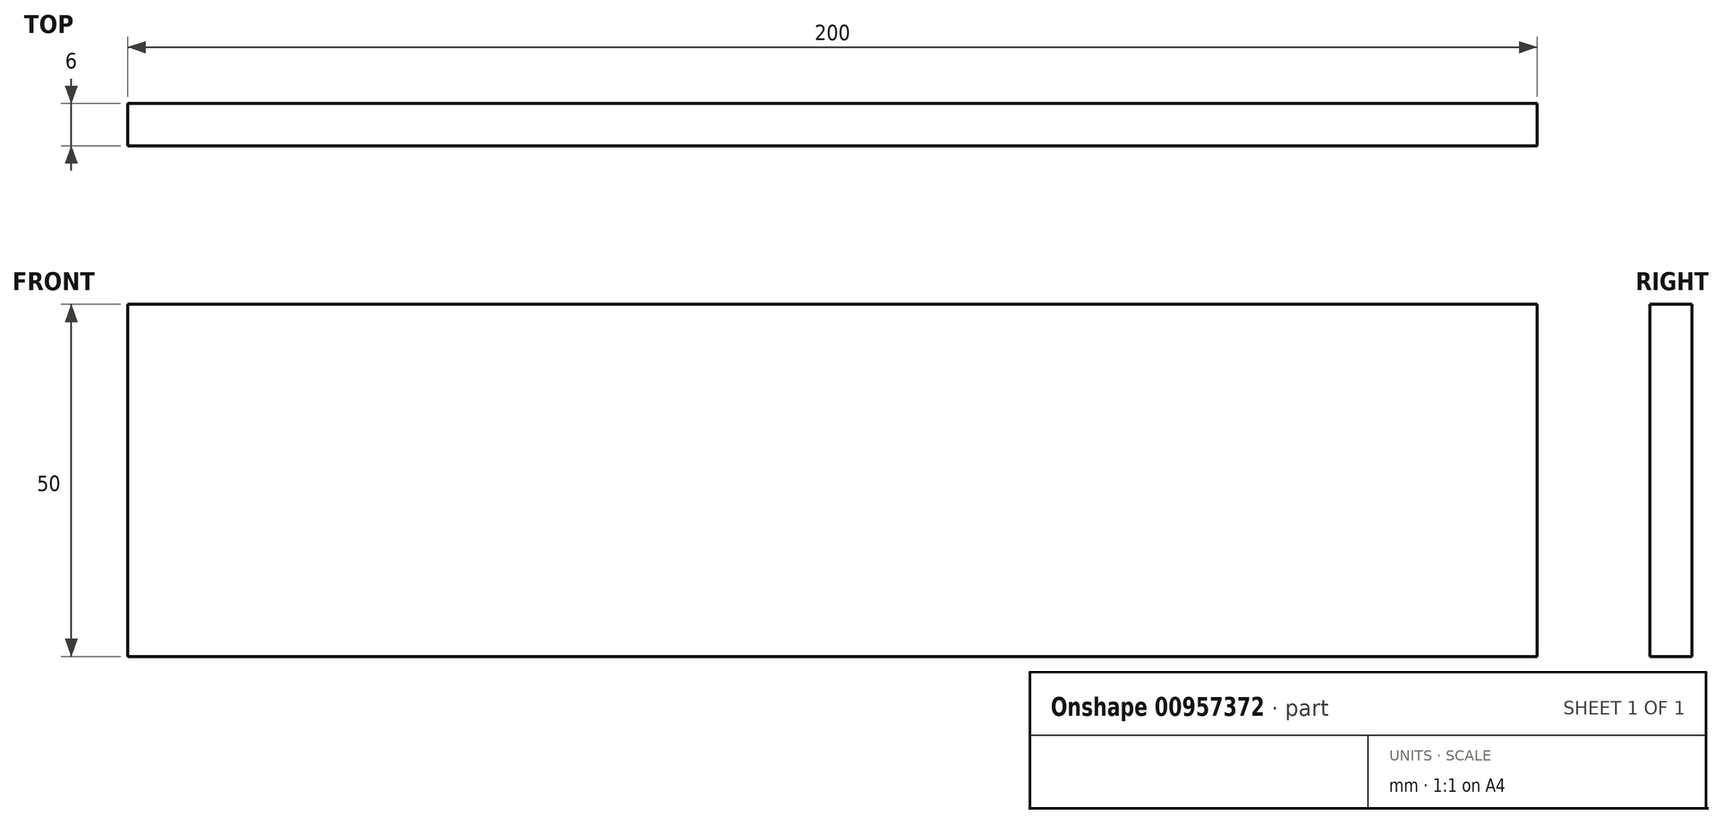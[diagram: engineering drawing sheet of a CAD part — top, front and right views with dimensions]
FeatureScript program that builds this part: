
annotation { "Feature Type Name" : "Feature", "Feature Type Description" : "" }
export const myFeature = defineFeature(function(context is Context, id is Id, definition is map)
    precondition{}
    {
        {
            var Q0;
            Q0=qCreatedBy(makeId("Front.planeOp"),FACE);
            var sketch = newSketch(context, id + "F0", { "sketchPlane" : qUnion([Q0])});
            skLineSegment(sketch, "E0.bottom", {"start": v(-68, 43.57) * mm, "end": v(132, 43.57) * mm});
            skLineSegment(sketch, "E0.top", {"start": v(-68, -6.43) * mm, "end": v(132, -6.43) * mm});
            skLineSegment(sketch, "E0.left", {"start": v(-68, 43.57) * mm, "end": v(-68, -6.43) * mm});
            skLineSegment(sketch, "E0.right", {"start": v(132, 43.57) * mm, "end": v(132, -6.43) * mm});
            skSolve(sketch);
        }
        {
            var Q0;
            Q0 = qSketchRegion(id + "F0", true);
            extrude(context, id + "F1", {"entities" : qUnion([Q0]), "depth" : 6 * mm, "offsetDistance" : 25 * mm});
        }
    });
